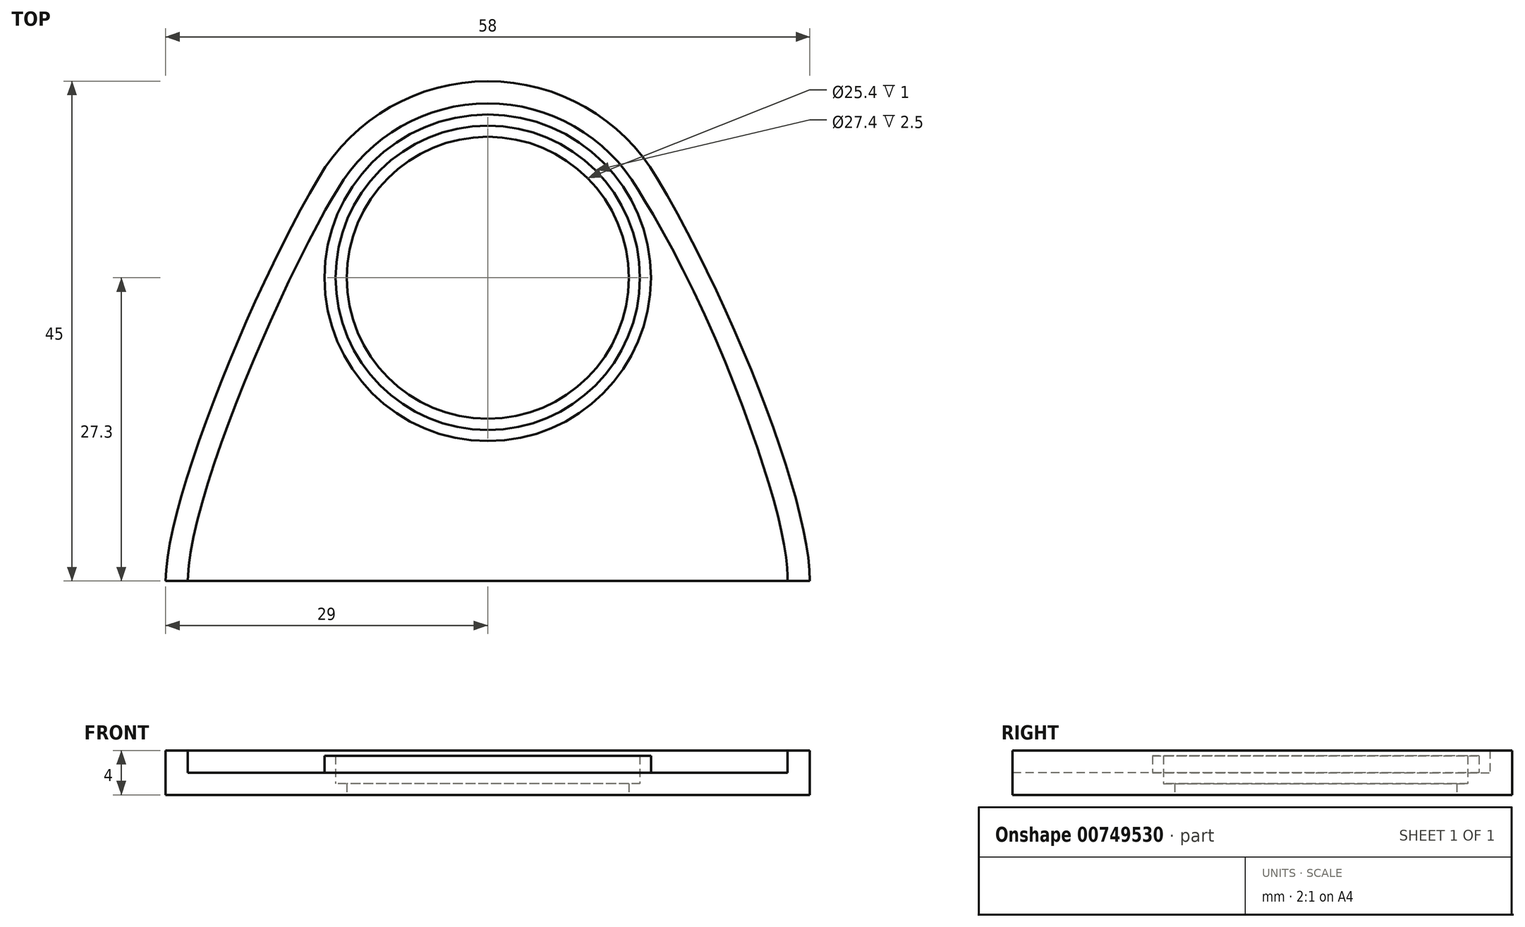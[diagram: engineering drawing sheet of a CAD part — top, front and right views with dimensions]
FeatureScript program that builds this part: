
annotation { "Feature Type Name" : "Feature", "Feature Type Description" : "" }
export const myFeature = defineFeature(function(context is Context, id is Id, definition is map)
    precondition{}
    {
        {
            var Q0;
            Q0=qCreatedBy(makeId("Top.planeOp"),FACE);
            var sketch = newSketch(context, id + "F0", { "sketchPlane" : qUnion([Q0])});
            skArc(sketch, "E0", {"start": v(15.25, 66.28) * mm, "mid": v(0, 75) * mm, "end": v(-15.25, 66.28) * mm});
            skCircle(sketch, "E1", {"center": v(0, 57.3) * mm, "radius": 12.7 * mm});
            skFitSpline(sketch, "E2", {"points": [v(-15.25, 66.28) * mm, v(-29, 30) * mm], "startDerivative": vector(-17.92, -30.43) * mm, "endDerivative": vector(0, -21.56) * mm});
            skFitSpline(sketch, "E3", {"points": [v(15.25, 66.28) * mm, v(29, 30) * mm], "startDerivative": vector(21.03, -35.71) * mm, "endDerivative": vector(0, -21.56) * mm});
            skLineSegment(sketch, "E4", {"start": v(-27, 30) * mm, "end": v(-29, 30) * mm});
            skLineSegment(sketch, "E5", {"start": v(27, 30) * mm, "end": v(29, 30) * mm});
            skLineSegment(sketch, "E6", {"start": v(-29, 30) * mm, "end": v(29, 30) * mm});
            skSolve(sketch);
        }
        {
            var Q0;
            Q0=makeQuery(id+"F0.imprint","IMPRINT",FACE,{"disambiguationData":[TD([[makeQuery(id+"F0.imprint","IMPRINT",EDGE,{"derivedFrom":sQuery(id+"F0.wireOp",EDGE,"E0")}),1.0]])]});
            extrude(context, id + "F1", {"entities" : qUnion([Q0]), "depth" : 2 * mm, "offsetDistance" : 25 * mm});
        }
        {
            var Q0;
            Q0=makeQuery(id+"F1.opExtrude","CAP_FACE",FACE,{"disambiguationData":[OSD([sQuery(id+"F0.wireOp",EDGE,"rKy58ZlB-kP61-Ok1W-jxmB-2eYKyQ9vMdYR"),sQuery(id+"F0.wireOp",EDGE,"0Ro1BS0Q-2mgt-ZydI-AfPz-EH0e96b9fWh7"),sQuery(id+"F0.wireOp",EDGE,"E1"),sQuery(id+"F0.wireOp",EDGE,"87762f92-a82d-4736-8b2d-cb61234f6977.0"),sQuery(id+"F0.wireOp",EDGE,"87762f92-a82d-4736-8b2d-cb61234f6977.2"),sQuery(id+"F0.wireOp",EDGE,"87762f92-a82d-4736-8b2d-cb61234f6977.3"),sQuery(id+"F0.wireOp",EDGE,"87762f92-a82d-4736-8b2d-cb61234f6977.5"),sQuery(id+"F0.wireOp",EDGE,"E4"),sQuery(id+"F0.wireOp",EDGE,"E5"),sQuery(id+"F0.wireOp",EDGE,"OBthIzAU-zjxL-SYiB-24dl-3B8FTxSEXE3T"),sQuery(id+"F0.wireOp",EDGE,"hQ1LHbks-fRvT-trK1-pk5m-avV33pfGG9a5")])],"isStart":false});
            var sketch = newSketch(context, id + "F2", { "sketchPlane" : qUnion([Q0])});
            skCircle(sketch, "E7", {"center": v(0, 57.3) * mm, "radius": 13.7 * mm});
            skCircle(sketch, "E8", {"center": v(0, 57.3) * mm, "radius": 14.7 * mm});
            skSolve(sketch);
        }
        {
            var Q0;
            Q0=makeQuery(id+"F2.imprint","IMPRINT",FACE,{"disambiguationData":[TD([[makeQuery(id+"F2.imprint","IMPRINT",EDGE,{"derivedFrom":sQuery(id+"F2.wireOp",EDGE,"E7")}),-1.0]])]});
            extrude(context, id + "F3", {"entities" : qUnion([Q0]), "operationType" : NewBodyOperationType.ADD, "depth" : 1.5 * mm, "offsetDistance" : 25 * mm});
        }
        {
            var Q0;
            {var subQ0=sQuery(id+"F0.wireOp",EDGE,"E1");Q0=makeQuery(id+"F3.boolean.opBoolean","SPLIT",FACE,{"disambiguationData":[TD([makeQuery(id+"F1.opExtrude","SWEPT_FACE",FACE,{"disambiguationData":[OSD([subQ0])]})])],"derivedFrom":makeQuery(id+"F1.opExtrude","CAP_FACE",FACE,{"disambiguationData":[OSD([sQuery(id+"F0.wireOp",EDGE,"rKy58ZlB-kP61-Ok1W-jxmB-2eYKyQ9vMdYR"),sQuery(id+"F0.wireOp",EDGE,"0Ro1BS0Q-2mgt-ZydI-AfPz-EH0e96b9fWh7"),subQ0,sQuery(id+"F0.wireOp",EDGE,"87762f92-a82d-4736-8b2d-cb61234f6977.0"),sQuery(id+"F0.wireOp",EDGE,"87762f92-a82d-4736-8b2d-cb61234f6977.2"),sQuery(id+"F0.wireOp",EDGE,"87762f92-a82d-4736-8b2d-cb61234f6977.3"),sQuery(id+"F0.wireOp",EDGE,"87762f92-a82d-4736-8b2d-cb61234f6977.5"),sQuery(id+"F0.wireOp",EDGE,"E4"),sQuery(id+"F0.wireOp",EDGE,"E5"),sQuery(id+"F0.wireOp",EDGE,"OBthIzAU-zjxL-SYiB-24dl-3B8FTxSEXE3T"),sQuery(id+"F0.wireOp",EDGE,"hQ1LHbks-fRvT-trK1-pk5m-avV33pfGG9a5")])],"isStart":false})});}
            extrude(context, id + "F4", {"entities" : qUnion([Q0]), "operationType" : NewBodyOperationType.REMOVE, "oppositeDirection" : true, "depth" : 1 * mm, "offsetDistance" : 25 * mm});
        }
        {
            var Q0;
            {var subQ0=sQuery(id+"F0.wireOp",EDGE,"E6");var subQ1=sQuery(id+"F0.wireOp",EDGE,"E2");var subQ2=sQuery(id+"F0.wireOp",EDGE,"E3");var subQ3=sQuery(id+"F0.wireOp",EDGE,"E0");Q0=makeQuery(id+"F3.boolean.opBoolean","SPLIT",FACE,{"disambiguationData":[TD([makeQuery(id+"F1.opExtrude","SWEPT_FACE",FACE,{"disambiguationData":[OSD([subQ3])]})])],"derivedFrom":makeQuery(id+"F1.opExtrude","CAP_FACE",FACE,{"disambiguationData":[OSD([subQ3,sQuery(id+"F0.wireOp",EDGE,"E1"),subQ1,subQ2,subQ0])],"isStart":false})});}
            var sketch = newSketch(context, id + "F5", { "sketchPlane" : qUnion([Q0])});
            skLineSegment(sketch, "E9", {"start": v(-27, 30) * mm, "end": v(27, 30) * mm});
            skFitSpline(sketch, "E10.0", {"points": [v(-13.53, 65.27) * mm, v(-14.25, 64.04) * mm, v(-15.77, 61.28) * mm, v(-18.12, 56.55) * mm, v(-20.42, 51.46) * mm, v(-22.55, 46.28) * mm, v(-24.4, 41.25) * mm, v(-25.85, 36.62) * mm, v(-26.63, 33.33) * mm, v(-26.95, 31.21) * mm, v(-27, 30.36) * mm, v(-27, 30) * mm]});
            skArc(sketch, "E10.1", {"start": v(13.53, 65.27) * mm, "mid": v(0, 73) * mm, "end": v(-13.53, 65.27) * mm});
            skFitSpline(sketch, "E10.2", {"points": [v(13.53, 65.27) * mm, v(15.25, 62.35) * mm, v(18.67, 55.84) * mm, v(22.37, 47.22) * mm, v(24.67, 40.8) * mm, v(25.98, 36.41) * mm, v(26.68, 33.28) * mm, v(26.96, 31.22) * mm, v(27, 30.37) * mm, v(27, 30) * mm]});
            skSolve(sketch);
        }
        {
            var Q0;
            {var subQ1=sQuery(id+"F5.wireOp",EDGE,"E10.0");Q0=makeQuery(id+"F5.imprint","IMPRINT",FACE,{"disambiguationData":[TD([[makeQuery(id+"F5.imprint","IMPRINT",EDGE,{"derivedFrom":subQ1}),-1.0]])]});}
            extrude(context, id + "F6", {"entities" : qUnion([Q0]), "operationType" : NewBodyOperationType.ADD, "depth" : 2 * mm, "offsetDistance" : 25 * mm});
        }
    });
